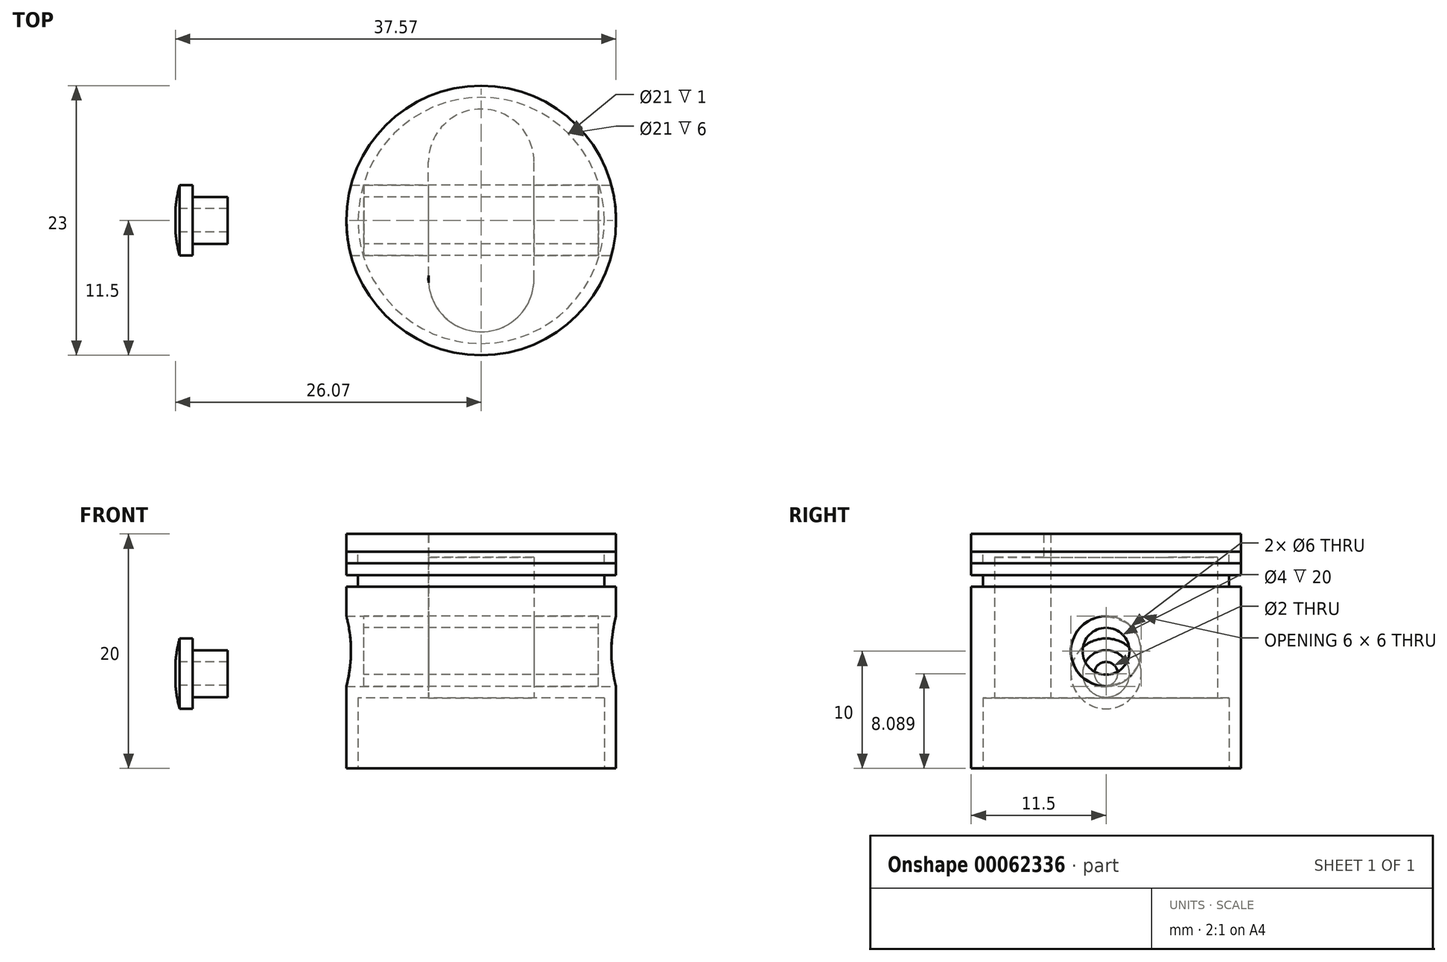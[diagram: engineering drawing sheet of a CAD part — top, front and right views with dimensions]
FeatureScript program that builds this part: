
annotation { "Feature Type Name" : "Feature", "Feature Type Description" : "" }
export const myFeature = defineFeature(function(context is Context, id is Id, definition is map)
    precondition{}
    {
        {
            var Q0;
            Q0=qCreatedBy(makeId("Top.planeOp"),FACE);
            var sketch = newSketch(context, id + "F0", { "sketchPlane" : qUnion([Q0])});
            skCircle(sketch, "E0", {"center": v(0, 0) * mm, "radius": 11.5 * mm});
            skLineSegment(sketch, "E1", {"start": v(0, 11.5) * mm, "end": v(0, -11.5) * mm});
            skCircle(sketch, "E2", {"center": v(0, -5) * mm, "radius": 4.5 * mm});
            skLineSegment(sketch, "E3", {"start": v(-11.5, 0) * mm, "end": v(11.5, 0) * mm});
            skCircle(sketch, "E4.MirrorC", {"center": v(0, 5) * mm, "radius": 4.5 * mm});
            skLineSegment(sketch, "E5", {"start": v(-4.49, -5.3) * mm, "end": v(-4.5, 5) * mm});
            skLineSegment(sketch, "E6", {"start": v(4.5, -5) * mm, "end": v(4.5, 5) * mm});
            skCircle(sketch, "E7", {"center": v(0, 0) * mm, "radius": 10.5 * mm});
            skSolve(sketch);
        }
        {
            var Q0;
            {var subQ0=sQuery(id+"F0.wireOp",EDGE,"E1");var subQ1=sQuery(id+"F0.wireOp",EDGE,"E0");var subQ2=makeQuery(id+"F0.imprint","INTERSECT",VERTEX,{"disambiguationData":[OD(0.0)],"derivedFrom":[subQ1,subQ0]});Q0=makeQuery(id+"F0.imprint","IMPRINT",FACE,{"disambiguationData":[TD([[makeQuery(id+"F0.imprint","IMPRINT",EDGE,{"disambiguationData":[TD([[subQ2,-1.0]])],"derivedFrom":subQ1}),1.0]])]});}
            var Q1;
            {var subQ5=sQuery(id+"F0.wireOp",EDGE,"E7");var subQ6=sQuery(id+"F0.wireOp",EDGE,"E1");var subQ7=makeQuery(id+"F0.imprint","INTERSECT",VERTEX,{"disambiguationData":[OD(0.0)],"derivedFrom":[subQ6,subQ5]});Q1=makeQuery(id+"F0.imprint","IMPRINT",FACE,{"disambiguationData":[TD([[makeQuery(id+"F0.imprint","IMPRINT",EDGE,{"disambiguationData":[TD([[subQ7,-1.0]])],"derivedFrom":subQ6}),-1.0]])]});}
            var Q2;
            {var subQ0=sQuery(id+"F0.wireOp",EDGE,"E4.MirrorC");var subQ1=sQuery(id+"F0.wireOp",EDGE,"E1");var subQ2=makeQuery(id+"F0.imprint","INTERSECT",VERTEX,{"disambiguationData":[OD(1.0)],"derivedFrom":[subQ1,subQ0]});Q2=makeQuery(id+"F0.imprint","IMPRINT",FACE,{"disambiguationData":[TD([[makeQuery(id+"F0.imprint","IMPRINT",EDGE,{"disambiguationData":[TD([[subQ2,-1.0]])],"derivedFrom":subQ1}),-1.0]])]});}
            var Q3;
            {var subQ0=sQuery(id+"F0.wireOp",EDGE,"E4.MirrorC");var subQ1=sQuery(id+"F0.wireOp",EDGE,"E1");var subQ2=makeQuery(id+"F0.imprint","INTERSECT",VERTEX,{"disambiguationData":[OD(0.0)],"derivedFrom":[subQ1,subQ0]});Q3=makeQuery(id+"F0.imprint","IMPRINT",FACE,{"disambiguationData":[TD([[makeQuery(id+"F0.imprint","IMPRINT",EDGE,{"disambiguationData":[TD([[subQ2,-1.0]])],"derivedFrom":subQ1}),-1.0]])]});}
            var Q4;
            {var subQ0=sQuery(id+"F0.wireOp",EDGE,"E4.MirrorC");var subQ1=sQuery(id+"F0.wireOp",EDGE,"E1");var subQ2=makeQuery(id+"F0.imprint","INTERSECT",VERTEX,{"disambiguationData":[OD(0.0)],"derivedFrom":[subQ1,subQ0]});Q4=makeQuery(id+"F0.imprint","IMPRINT",FACE,{"disambiguationData":[TD([[makeQuery(id+"F0.imprint","IMPRINT",EDGE,{"disambiguationData":[TD([[subQ2,-1.0]])],"derivedFrom":subQ1}),1.0]])]});}
            var Q5;
            {var subQ0=sQuery(id+"F0.wireOp",EDGE,"E1");var subQ1=sQuery(id+"F0.wireOp",EDGE,"E0");var subQ2=makeQuery(id+"F0.imprint","INTERSECT",VERTEX,{"disambiguationData":[OD(0.0)],"derivedFrom":[subQ1,subQ0]});Q5=makeQuery(id+"F0.imprint","IMPRINT",FACE,{"disambiguationData":[TD([[makeQuery(id+"F0.imprint","IMPRINT",EDGE,{"disambiguationData":[TD([[subQ2,1.0]])],"derivedFrom":subQ1}),1.0]])]});}
            var Q6;
            {var subQ0=sQuery(id+"F0.wireOp",EDGE,"E3");var subQ1=sQuery(id+"F0.wireOp",EDGE,"E1");var subQ2=makeQuery(id+"F0.imprint","INTERSECT",VERTEX,{"derivedFrom":[subQ1,subQ0]});Q6=makeQuery(id+"F0.imprint","IMPRINT",FACE,{"disambiguationData":[TD([[makeQuery(id+"F0.imprint","IMPRINT",EDGE,{"disambiguationData":[TD([[subQ2,-1.0]])],"derivedFrom":subQ1}),1.0]])]});}
            var Q7;
            {var subQ1=sQuery(id+"F0.wireOp",EDGE,"E2");var subQ5=sQuery(id+"F0.wireOp",EDGE,"E1");var subQ6=makeQuery(id+"F0.imprint","INTERSECT",VERTEX,{"disambiguationData":[OD(1.0)],"derivedFrom":[subQ5,subQ1]});Q7=makeQuery(id+"F0.imprint","IMPRINT",FACE,{"disambiguationData":[TD([[makeQuery(id+"F0.imprint","IMPRINT",EDGE,{"disambiguationData":[TD([[subQ6,-1.0]])],"derivedFrom":subQ5}),1.0]])]});}
            var Q8;
            {var subQ0=sQuery(id+"F0.wireOp",EDGE,"E1");var subQ1=sQuery(id+"F0.wireOp",EDGE,"E0");var subQ2=makeQuery(id+"F0.imprint","INTERSECT",VERTEX,{"disambiguationData":[OD(1.0)],"derivedFrom":[subQ1,subQ0]});Q8=makeQuery(id+"F0.imprint","IMPRINT",FACE,{"disambiguationData":[TD([[makeQuery(id+"F0.imprint","IMPRINT",EDGE,{"disambiguationData":[TD([[subQ2,1.0]])],"derivedFrom":subQ1}),1.0]])]});}
            var Q9;
            {var subQ5=sQuery(id+"F0.wireOp",EDGE,"E2");var subQ8=sQuery(id+"F0.wireOp",EDGE,"E1");var subQ9=makeQuery(id+"F0.imprint","INTERSECT",VERTEX,{"disambiguationData":[OD(1.0)],"derivedFrom":[subQ8,subQ5]});Q9=makeQuery(id+"F0.imprint","IMPRINT",FACE,{"disambiguationData":[TD([[makeQuery(id+"F0.imprint","IMPRINT",EDGE,{"disambiguationData":[TD([[subQ9,-1.0]])],"derivedFrom":subQ8}),-1.0]])]});}
            var Q10;
            {var subQ0=sQuery(id+"F0.wireOp",EDGE,"E3");var subQ1=sQuery(id+"F0.wireOp",EDGE,"E1");var subQ2=makeQuery(id+"F0.imprint","INTERSECT",VERTEX,{"derivedFrom":[subQ1,subQ0]});Q10=makeQuery(id+"F0.imprint","IMPRINT",FACE,{"disambiguationData":[TD([[makeQuery(id+"F0.imprint","IMPRINT",EDGE,{"disambiguationData":[TD([[subQ2,-1.0]])],"derivedFrom":subQ1}),-1.0]])]});}
            var Q11;
            {var subQ0=sQuery(id+"F0.wireOp",EDGE,"E2");var subQ1=sQuery(id+"F0.wireOp",EDGE,"E1");var subQ2=makeQuery(id+"F0.imprint","INTERSECT",VERTEX,{"disambiguationData":[OD(0.0)],"derivedFrom":[subQ1,subQ0]});Q11=makeQuery(id+"F0.imprint","IMPRINT",FACE,{"disambiguationData":[TD([[makeQuery(id+"F0.imprint","IMPRINT",EDGE,{"disambiguationData":[TD([[subQ2,-1.0]])],"derivedFrom":subQ1}),-1.0]])]});}
            var Q12;
            {var subQ0=sQuery(id+"F0.wireOp",EDGE,"E2");var subQ1=sQuery(id+"F0.wireOp",EDGE,"E1");var subQ2=makeQuery(id+"F0.imprint","INTERSECT",VERTEX,{"disambiguationData":[OD(0.0)],"derivedFrom":[subQ1,subQ0]});Q12=makeQuery(id+"F0.imprint","IMPRINT",FACE,{"disambiguationData":[TD([[makeQuery(id+"F0.imprint","IMPRINT",EDGE,{"disambiguationData":[TD([[subQ2,-1.0]])],"derivedFrom":subQ1}),1.0]])]});}
            var Q13;
            {var subQ0=sQuery(id+"F0.wireOp",EDGE,"E1");var subQ1=sQuery(id+"F0.wireOp",EDGE,"E0");var subQ2=makeQuery(id+"F0.imprint","INTERSECT",VERTEX,{"disambiguationData":[OD(1.0)],"derivedFrom":[subQ1,subQ0]});Q13=makeQuery(id+"F0.imprint","IMPRINT",FACE,{"disambiguationData":[TD([[makeQuery(id+"F0.imprint","IMPRINT",EDGE,{"disambiguationData":[TD([[subQ2,-1.0]])],"derivedFrom":subQ1}),1.0]])]});}
            var Q14;
            {var subQ5=sQuery(id+"F0.wireOp",EDGE,"E1");var subQ7=sQuery(id+"F0.wireOp",EDGE,"E7");var subQ9=makeQuery(id+"F0.imprint","INTERSECT",VERTEX,{"disambiguationData":[OD(0.0)],"derivedFrom":[subQ5,subQ7]});Q14=makeQuery(id+"F0.imprint","IMPRINT",FACE,{"disambiguationData":[TD([[makeQuery(id+"F0.imprint","IMPRINT",EDGE,{"disambiguationData":[TD([[subQ9,-1.0]])],"derivedFrom":subQ5}),1.0]])]});}
            var Q15;
            {var subQ0=sQuery(id+"F0.wireOp",EDGE,"E4.MirrorC");var subQ1=sQuery(id+"F0.wireOp",EDGE,"E1");var subQ2=makeQuery(id+"F0.imprint","INTERSECT",VERTEX,{"disambiguationData":[OD(1.0)],"derivedFrom":[subQ1,subQ0]});Q15=makeQuery(id+"F0.imprint","IMPRINT",FACE,{"disambiguationData":[TD([[makeQuery(id+"F0.imprint","IMPRINT",EDGE,{"disambiguationData":[TD([[subQ2,-1.0]])],"derivedFrom":subQ1}),1.0]])]});}
            extrude(context, id + "F1", {"entities" : qUnion([Q0, Q1, Q2, Q3, Q4, Q5, Q6, Q7, Q8, Q9, Q10, Q11, Q12, Q13, Q14, Q15]), "depth" : 20 * mm});
        }
        {
            var Q0;
            {var subQ0=sQuery(id+"F0.wireOp",EDGE,"E2");var subQ1=sQuery(id+"F0.wireOp",EDGE,"E1");var subQ2=makeQuery(id+"F0.imprint","INTERSECT",VERTEX,{"disambiguationData":[OD(0.0)],"derivedFrom":[subQ1,subQ0]});Q0=makeQuery(id+"F0.imprint","IMPRINT",FACE,{"disambiguationData":[TD([[makeQuery(id+"F0.imprint","IMPRINT",EDGE,{"disambiguationData":[TD([[subQ2,-1.0]])],"derivedFrom":subQ1}),-1.0]])]});}
            var Q1;
            {var subQ0=sQuery(id+"F0.wireOp",EDGE,"E2");var subQ1=sQuery(id+"F0.wireOp",EDGE,"E1");var subQ2=makeQuery(id+"F0.imprint","INTERSECT",VERTEX,{"disambiguationData":[OD(0.0)],"derivedFrom":[subQ1,subQ0]});Q1=makeQuery(id+"F0.imprint","IMPRINT",FACE,{"disambiguationData":[TD([[makeQuery(id+"F0.imprint","IMPRINT",EDGE,{"disambiguationData":[TD([[subQ2,-1.0]])],"derivedFrom":subQ1}),1.0]])]});}
            var Q2;
            {var subQ0=sQuery(id+"F0.wireOp",EDGE,"E3");var subQ1=sQuery(id+"F0.wireOp",EDGE,"E1");var subQ2=makeQuery(id+"F0.imprint","INTERSECT",VERTEX,{"derivedFrom":[subQ1,subQ0]});Q2=makeQuery(id+"F0.imprint","IMPRINT",FACE,{"disambiguationData":[TD([[makeQuery(id+"F0.imprint","IMPRINT",EDGE,{"disambiguationData":[TD([[subQ2,-1.0]])],"derivedFrom":subQ1}),1.0]])]});}
            var Q3;
            {var subQ0=sQuery(id+"F0.wireOp",EDGE,"E4.MirrorC");var subQ1=sQuery(id+"F0.wireOp",EDGE,"E1");var subQ2=makeQuery(id+"F0.imprint","INTERSECT",VERTEX,{"disambiguationData":[OD(1.0)],"derivedFrom":[subQ1,subQ0]});Q3=makeQuery(id+"F0.imprint","IMPRINT",FACE,{"disambiguationData":[TD([[makeQuery(id+"F0.imprint","IMPRINT",EDGE,{"disambiguationData":[TD([[subQ2,-1.0]])],"derivedFrom":subQ1}),1.0]])]});}
            var Q4;
            {var subQ0=sQuery(id+"F0.wireOp",EDGE,"E4.MirrorC");var subQ1=sQuery(id+"F0.wireOp",EDGE,"E1");var subQ2=makeQuery(id+"F0.imprint","INTERSECT",VERTEX,{"disambiguationData":[OD(0.0)],"derivedFrom":[subQ1,subQ0]});Q4=makeQuery(id+"F0.imprint","IMPRINT",FACE,{"disambiguationData":[TD([[makeQuery(id+"F0.imprint","IMPRINT",EDGE,{"disambiguationData":[TD([[subQ2,-1.0]])],"derivedFrom":subQ1}),1.0]])]});}
            var Q5;
            {var subQ0=sQuery(id+"F0.wireOp",EDGE,"E4.MirrorC");var subQ1=sQuery(id+"F0.wireOp",EDGE,"E1");var subQ2=makeQuery(id+"F0.imprint","INTERSECT",VERTEX,{"disambiguationData":[OD(0.0)],"derivedFrom":[subQ1,subQ0]});Q5=makeQuery(id+"F0.imprint","IMPRINT",FACE,{"disambiguationData":[TD([[makeQuery(id+"F0.imprint","IMPRINT",EDGE,{"disambiguationData":[TD([[subQ2,-1.0]])],"derivedFrom":subQ1}),-1.0]])]});}
            var Q6;
            {var subQ0=sQuery(id+"F0.wireOp",EDGE,"E3");var subQ1=sQuery(id+"F0.wireOp",EDGE,"E1");var subQ2=makeQuery(id+"F0.imprint","INTERSECT",VERTEX,{"derivedFrom":[subQ1,subQ0]});Q6=makeQuery(id+"F0.imprint","IMPRINT",FACE,{"disambiguationData":[TD([[makeQuery(id+"F0.imprint","IMPRINT",EDGE,{"disambiguationData":[TD([[subQ2,-1.0]])],"derivedFrom":subQ1}),-1.0]])]});}
            var Q7;
            {var subQ0=sQuery(id+"F0.wireOp",EDGE,"E4.MirrorC");var subQ1=sQuery(id+"F0.wireOp",EDGE,"E1");var subQ2=makeQuery(id+"F0.imprint","INTERSECT",VERTEX,{"disambiguationData":[OD(1.0)],"derivedFrom":[subQ1,subQ0]});Q7=makeQuery(id+"F0.imprint","IMPRINT",FACE,{"disambiguationData":[TD([[makeQuery(id+"F0.imprint","IMPRINT",EDGE,{"disambiguationData":[TD([[subQ2,-1.0]])],"derivedFrom":subQ1}),-1.0]])]});}
            extrude(context, id + "F2", {"entities" : qUnion([Q0, Q1, Q2, Q3, Q4, Q5, Q6, Q7]), "operationType" : NewBodyOperationType.REMOVE, "depth" : 18 * mm});
        }
        {
            var Q0;
            {var subQ5=sQuery(id+"F0.wireOp",EDGE,"E2");var subQ8=sQuery(id+"F0.wireOp",EDGE,"E1");var subQ9=makeQuery(id+"F0.imprint","INTERSECT",VERTEX,{"disambiguationData":[OD(1.0)],"derivedFrom":[subQ8,subQ5]});Q0=makeQuery(id+"F0.imprint","IMPRINT",FACE,{"disambiguationData":[TD([[makeQuery(id+"F0.imprint","IMPRINT",EDGE,{"disambiguationData":[TD([[subQ9,-1.0]])],"derivedFrom":subQ8}),-1.0]])]});}
            var Q1;
            {var subQ1=sQuery(id+"F0.wireOp",EDGE,"E2");var subQ5=sQuery(id+"F0.wireOp",EDGE,"E1");var subQ6=makeQuery(id+"F0.imprint","INTERSECT",VERTEX,{"disambiguationData":[OD(1.0)],"derivedFrom":[subQ5,subQ1]});Q1=makeQuery(id+"F0.imprint","IMPRINT",FACE,{"disambiguationData":[TD([[makeQuery(id+"F0.imprint","IMPRINT",EDGE,{"disambiguationData":[TD([[subQ6,-1.0]])],"derivedFrom":subQ5}),1.0]])]});}
            var Q2;
            {var subQ5=sQuery(id+"F0.wireOp",EDGE,"E1");var subQ7=sQuery(id+"F0.wireOp",EDGE,"E7");var subQ9=makeQuery(id+"F0.imprint","INTERSECT",VERTEX,{"disambiguationData":[OD(0.0)],"derivedFrom":[subQ5,subQ7]});Q2=makeQuery(id+"F0.imprint","IMPRINT",FACE,{"disambiguationData":[TD([[makeQuery(id+"F0.imprint","IMPRINT",EDGE,{"disambiguationData":[TD([[subQ9,-1.0]])],"derivedFrom":subQ5}),1.0]])]});}
            var Q3;
            {var subQ5=sQuery(id+"F0.wireOp",EDGE,"E7");var subQ6=sQuery(id+"F0.wireOp",EDGE,"E1");var subQ7=makeQuery(id+"F0.imprint","INTERSECT",VERTEX,{"disambiguationData":[OD(0.0)],"derivedFrom":[subQ6,subQ5]});Q3=makeQuery(id+"F0.imprint","IMPRINT",FACE,{"disambiguationData":[TD([[makeQuery(id+"F0.imprint","IMPRINT",EDGE,{"disambiguationData":[TD([[subQ7,-1.0]])],"derivedFrom":subQ6}),-1.0]])]});}
            extrude(context, id + "F3", {"entities" : qUnion([Q0, Q1, Q2, Q3]), "operationType" : NewBodyOperationType.REMOVE, "depth" : 6 * mm});
        }
        {
            var Q0;
            Q0=qCreatedBy(makeId("Right.planeOp"),FACE);
            var sketch = newSketch(context, id + "F4", { "sketchPlane" : qUnion([Q0])});
            skLineSegment(sketch, "E8", {"start": v(0, 20) * mm, "end": v(0, 0) * mm});
            skCircle(sketch, "E9", {"center": v(0, 10) * mm, "radius": 3 * mm});
            skSolve(sketch);
        }
        {
            var Q0;
            {var subQ0=sQuery(id+"F4.wireOp",EDGE,"E9");var subQ1=sQuery(id+"F4.wireOp",EDGE,"E8");var subQ2=makeQuery(id+"F4.imprint","INTERSECT",VERTEX,{"disambiguationData":[OD(0.0)],"derivedFrom":[subQ1,subQ0]});Q0=makeQuery(id+"F4.imprint","IMPRINT",FACE,{"disambiguationData":[TD([[makeQuery(id+"F4.imprint","IMPRINT",EDGE,{"disambiguationData":[TD([[subQ2,1.0]])],"derivedFrom":subQ1}),1.0]])]});}
            var Q1;
            {var subQ0=sQuery(id+"F4.wireOp",EDGE,"E9");var subQ1=sQuery(id+"F4.wireOp",EDGE,"E8");var subQ2=makeQuery(id+"F4.imprint","INTERSECT",VERTEX,{"disambiguationData":[OD(0.0)],"derivedFrom":[subQ1,subQ0]});Q1=makeQuery(id+"F4.imprint","IMPRINT",FACE,{"disambiguationData":[TD([[makeQuery(id+"F4.imprint","IMPRINT",EDGE,{"disambiguationData":[TD([[subQ2,1.0]])],"derivedFrom":subQ1}),-1.0]])]});}
            var Q2;
            Q2=makeQuery(id+"F1.opExtrude","SWEPT_BODY",BODY,{"disambiguationData":[OSD([sQuery(id+"F0.wireOp",EDGE,"E0"),sQuery(id+"F0.wireOp",EDGE,"E2"),sQuery(id+"F0.wireOp",EDGE,"E5")])]});
            extrude(context, id + "F5", {"entities" : qUnion([Q0, Q1]), "operationType" : NewBodyOperationType.REMOVE, "oppositeDirection" : true, "endBoundEntityBody" : qUnion([Q2]), "depth" : 25 * mm, "symmetric" : true});
        }
        {
            var Q0;
            Q0=makeQuery(id+"F1.opExtrude","CAP_FACE",FACE,{"disambiguationData":[OSD([sQuery(id+"F0.wireOp",EDGE,"E0"),sQuery(id+"F0.wireOp",EDGE,"E2"),sQuery(id+"F0.wireOp",EDGE,"E5")])],"isStart":false});
            cPlane(context, id + "F6", {"entities" : qUnion([Q0]), "cplaneType" : CPlaneType.OFFSET, "offset" : 1.5 * mm, "oppositeDirection" : true, "width" : 150 * mm, "height" : 150 * mm});
        }
        {
            var Q0;
            Q0=qCreatedBy(id+"F6.planeOp",FACE);
            var sketch = newSketch(context, id + "F7", { "sketchPlane" : qUnion([Q0])});
            skCircle(sketch, "E10.0", {"center": v(0, 0) * mm, "radius": 11.5 * mm});
            skCircle(sketch, "E11", {"center": v(0, 0) * mm, "radius": 10.5 * mm});
            skSolve(sketch);
        }
        {
            var Q0;
            Q0=makeQuery(id+"F7.imprint","IMPRINT",FACE,{"disambiguationData":[TD([[makeQuery(id+"F7.imprint","IMPRINT",EDGE,{"derivedFrom":sQuery(id+"F7.wireOp",EDGE,"E10.0")}),1.0]])]});
            extrude(context, id + "F8", {"entities" : qUnion([Q0]), "operationType" : NewBodyOperationType.REMOVE, "oppositeDirection" : true, "depth" : 1 * mm});
        }
        {
            var Q0;
            Q0=qCreatedBy(id+"F6.planeOp",FACE);
            cPlane(context, id + "F9", {"entities" : qUnion([Q0]), "cplaneType" : CPlaneType.OFFSET, "offset" : 2 * mm, "oppositeDirection" : true, "width" : 150 * mm, "height" : 150 * mm});
        }
        {
            var Q0;
            Q0=qCreatedBy(id+"F9.planeOp",FACE);
            var sketch = newSketch(context, id + "F10", { "sketchPlane" : qUnion([Q0])});
            skCircle(sketch, "E12.0", {"center": v(0, 0) * mm, "radius": 11.5 * mm});
            skCircle(sketch, "E12.1", {"center": v(0, 0) * mm, "radius": 10.5 * mm});
            skSolve(sketch);
        }
        {
            var Q0;
            Q0=makeQuery(id+"F10.imprint","IMPRINT",FACE,{"disambiguationData":[TD([[makeQuery(id+"F10.imprint","IMPRINT",EDGE,{"derivedFrom":sQuery(id+"F10.wireOp",EDGE,"E12.0")}),1.0]])]});
            extrude(context, id + "F11", {"entities" : qUnion([Q0]), "operationType" : NewBodyOperationType.REMOVE, "oppositeDirection" : true, "depth" : 1 * mm});
        }
        {
            var Q0;
            Q0=makeQuery(id+"F7.imprint","IMPRINT",FACE,{"disambiguationData":[TD([[makeQuery(id+"F7.imprint","IMPRINT",EDGE,{"derivedFrom":sQuery(id+"F7.wireOp",EDGE,"E10.0")}),1.0]])]});
            extrude(context, id + "F12", {"entities" : qUnion([Q0]), "oppositeDirection" : true, "depth" : 1 * mm});
        }
        {
            var Q0;
            {var subQ0=sQuery(id+"F4.wireOp",EDGE,"E9");var subQ1=sQuery(id+"F4.wireOp",EDGE,"E8");var subQ2=makeQuery(id+"F4.imprint","INTERSECT",VERTEX,{"disambiguationData":[OD(0.0)],"derivedFrom":[subQ1,subQ0]});Q0=makeQuery(id+"F4.imprint","IMPRINT",FACE,{"disambiguationData":[TD([[makeQuery(id+"F4.imprint","IMPRINT",EDGE,{"disambiguationData":[TD([[subQ2,1.0]])],"derivedFrom":subQ1}),1.0]])]});}
            var sketch = newSketch(context, id + "F13", { "sketchPlane" : qUnion([Q0])});
            skCircle(sketch, "E13.0", {"center": v(0, 10) * mm, "radius": 3 * mm});
            skCircle(sketch, "E14", {"center": v(0, 10) * mm, "radius": 2 * mm});
            skSolve(sketch);
        }
        {
            var Q0;
            {var subQ0=sQuery(id+"F13.wireOp",EDGE,"E13.0");var subQ1=sQuery(id+"F4.wireOp",EDGE,"E9");var subQ2=sQuery(id+"F4.wireOp",EDGE,"E8");var subQ3=makeQuery(id+"F4.imprint","IMPRINT",EDGE,{"disambiguationData":[TD([[makeQuery(id+"F4.imprint","INTERSECT",VERTEX,{"disambiguationData":[OD(0.0)],"derivedFrom":[subQ2,subQ1]}),1.0]])],"derivedFrom":subQ2});var subQ4=makeQuery(id+"F13.imprint","INTERSECT",VERTEX,{"disambiguationData":[OD(0.0)],"derivedFrom":[subQ3,subQ0]});Q0=makeQuery(id+"F13.imprint","IMPRINT",FACE,{"disambiguationData":[TD([[makeQuery(id+"F13.imprint","IMPRINT",EDGE,{"disambiguationData":[TD([[subQ4,1.0]])],"derivedFrom":subQ0}),1.0]])]});}
            var Q1;
            {var subQ0=sQuery(id+"F13.wireOp",EDGE,"E13.0");var subQ1=sQuery(id+"F4.wireOp",EDGE,"E9");var subQ2=sQuery(id+"F4.wireOp",EDGE,"E8");var subQ3=makeQuery(id+"F4.imprint","IMPRINT",EDGE,{"disambiguationData":[TD([[makeQuery(id+"F4.imprint","INTERSECT",VERTEX,{"disambiguationData":[OD(0.0)],"derivedFrom":[subQ2,subQ1]}),1.0]])],"derivedFrom":subQ2});var subQ4=makeQuery(id+"F13.imprint","INTERSECT",VERTEX,{"disambiguationData":[OD(0.0)],"derivedFrom":[subQ3,subQ0]});Q1=makeQuery(id+"F13.imprint","IMPRINT",FACE,{"disambiguationData":[TD([[makeQuery(id+"F13.imprint","IMPRINT",EDGE,{"disambiguationData":[TD([[subQ4,-1.0]])],"derivedFrom":subQ0}),1.0]])]});}
            extrude(context, id + "F14", {"entities" : qUnion([Q0, Q1]), "depth" : 20 * mm, "symmetric" : true});
        }
        {
            var Q0;
            Q0=qCreatedBy(makeId("Front.planeOp"),FACE);
            var sketch = newSketch(context, id + "F15", { "sketchPlane" : qUnion([Q0])});
            skLineSegment(sketch, "E15", {"start": v(0, 6.09) * mm, "end": v(-10, 6.09) * mm});
            skLineSegment(sketch, "E16", {"start": v(-21.62, 8.09) * mm, "end": v(-21.62, 10.09) * mm});
            skLineSegment(sketch, "E17", {"start": v(-21.62, 10.09) * mm, "end": v(-24.62, 10.09) * mm});
            skLineSegment(sketch, "E18", {"start": v(-24.62, 10.09) * mm, "end": v(-24.62, 11.09) * mm});
            skLineSegment(sketch, "E19", {"start": v(-24.62, 11.09) * mm, "end": v(-25.72, 11.09) * mm});
            skLineSegment(sketch, "E20", {"start": v(-25.37, 8.09) * mm, "end": v(-26.12, 8.09) * mm});
            skLineSegment(sketch, "E21", {"start": v(-26.12, 8.09) * mm, "end": v(-14.62, 8.09) * mm});
            skPoint(sketch, "E21.endSnap0", {"position": v(-25.74, 8.09) * mm});
            skArc(sketch, "E22", {"start": v(-26.12, 8.09) * mm, "mid": v(-26.02, 9.6) * mm, "end": v(-25.72, 11.09) * mm});
            skLineSegment(sketch, "E23", {"start": v(-21.62, 9.09) * mm, "end": v(-26.07, 9.09) * mm});
            skSolve(sketch);
        }
        {
            var Q0;
            {var subQ1=sQuery(id+"F15.wireOp",EDGE,"E17");Q0=makeQuery(id+"F15.imprint","IMPRINT",FACE,{"disambiguationData":[TD([[makeQuery(id+"F15.imprint","IMPRINT",EDGE,{"derivedFrom":subQ1}),1.0]])]});}
            var Q1;
            Q1=sQuery(id+"F15.wireOp",EDGE,"E21");
            revolve(context, id + "F16", {"entities" : qUnion([Q0]), "axis" : qUnion([Q1]), "revolveType" : RevolveType.FULL});
        }
    });
